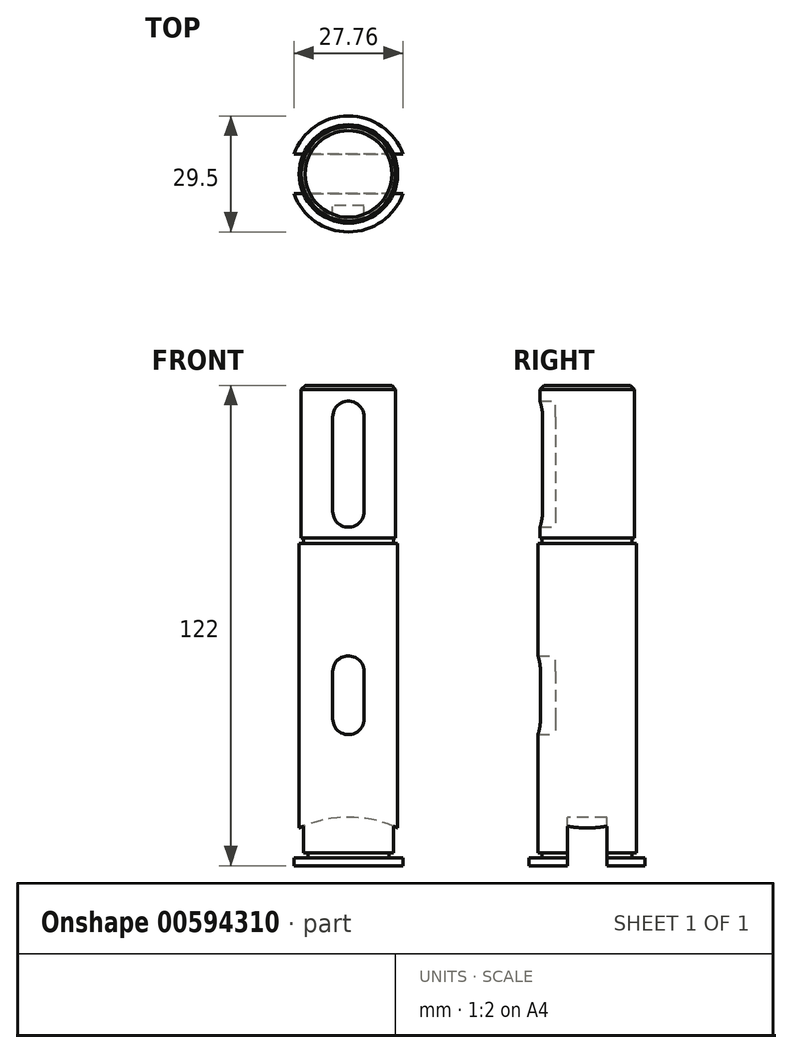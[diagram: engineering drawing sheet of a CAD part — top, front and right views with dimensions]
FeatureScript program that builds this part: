
annotation { "Feature Type Name" : "Feature", "Feature Type Description" : "" }
export const myFeature = defineFeature(function(context is Context, id is Id, definition is map)
    precondition{}
    {
        {
            var Q0;
            Q0=qCreatedBy(makeId("Front.planeOp"),FACE);
            var sketch = newSketch(context, id + "F0", { "sketchPlane" : qUnion([Q0])});
            skLineSegment(sketch, "E0", {"start": v(0, -2) * mm, "end": v(-14.75, -2) * mm});
            skLineSegment(sketch, "E1", {"start": v(-14.75, -2) * mm, "end": v(-14.75, 0) * mm});
            skLineSegment(sketch, "E2", {"start": v(-14.75, 0) * mm, "end": v(-11.45, 0) * mm});
            skLineSegment(sketch, "E3", {"start": v(-11.45, 0) * mm, "end": v(-11.45, 1.3) * mm});
            skLineSegment(sketch, "E4", {"start": v(-11.45, 1.3) * mm, "end": v(-12.5, 1.3) * mm});
            skLineSegment(sketch, "E5", {"start": v(-12.5, 1.3) * mm, "end": v(-12.5, 79.9) * mm});
            skLineSegment(sketch, "E6", {"start": v(-12.5, 79.9) * mm, "end": v(-11.45, 79.9) * mm});
            skLineSegment(sketch, "E7", {"start": v(-11.45, 79.9) * mm, "end": v(-11.45, 81.2) * mm});
            skLineSegment(sketch, "E8", {"start": v(-11.45, 81.2) * mm, "end": v(-12, 81.2) * mm});
            skLineSegment(sketch, "E9", {"start": v(-12, 81.2) * mm, "end": v(-12, 120) * mm});
            skLineSegment(sketch, "E10", {"start": v(-12, 120) * mm, "end": v(0, 120) * mm});
            skLineSegment(sketch, "E11", {"start": v(0, 120) * mm, "end": v(0, -2) * mm});
            skSolve(sketch);
        }
        {
            var Q0;
            Q0=makeQuery(id+"F0.imprint","IMPRINT",FACE,{"disambiguationData":[TD([[makeQuery(id+"F0.imprint","IMPRINT",EDGE,{"derivedFrom":sQuery(id+"F0.wireOp",EDGE,"E0")}),-1.0]])]});
            var Q1;
            Q1=sQuery(id+"F0.wireOp",EDGE,"E11");
            revolve(context, id + "F1", {"entities" : qUnion([Q0]), "axis" : qUnion([Q1]), "revolveType" : RevolveType.FULL});
        }
        {
            var Q0;
            Q0=qCreatedBy(makeId("Front.planeOp"),FACE);
            var sketch = newSketch(context, id + "F2", { "sketchPlane" : qUnion([Q0])});
            skCircle(sketch, "E12", {"center": v(0, -19.7) * mm, "radius": 30 * mm});
            skSolve(sketch);
        }
        {
            var Q0;
            Q0=makeQuery(id+"F2.imprint","IMPRINT",FACE,{"disambiguationData":[TD([[makeQuery(id+"F2.imprint","IMPRINT",EDGE,{"derivedFrom":sQuery(id+"F2.wireOp",EDGE,"E12")}),1.0]])]});
            extrude(context, id + "F3", {"entities" : qUnion([Q0]), "operationType" : NewBodyOperationType.REMOVE, "oppositeDirection" : true, "depth" : 5 * mm, "offsetDistance" : 25 * mm, "hasSecondDirection" : true, "secondDirectionOppositeDirection" : false, "secondDirectionDepth" : 5 * mm});
        }
        {
            var Q0;
            Q0=qCreatedBy(makeId("Front.planeOp"),FACE);
            cPlane(context, id + "F4", {"entities" : qUnion([Q0]), "cplaneType" : CPlaneType.OFFSET, "offset" : 8 * mm, "width" : 150 * mm, "height" : 150 * mm});
        }
        {
            var Q0;
            Q0=qCreatedBy(id+"F4.planeOp",FACE);
            var sketch = newSketch(context, id + "F5", { "sketchPlane" : qUnion([Q0])});
            skLineSegment(sketch, "E13.left", {"start": v(-4, 112) * mm, "end": v(-4, 88) * mm});
            skLineSegment(sketch, "E13.right", {"start": v(4, 112) * mm, "end": v(4, 88) * mm});
            skArc(sketch, "E14", {"start": v(4, 112) * mm, "mid": v(0, 116) * mm, "end": v(-4, 112) * mm});
            skArc(sketch, "E15", {"start": v(-4, 88) * mm, "mid": v(0, 84) * mm, "end": v(4, 88) * mm});
            skSolve(sketch);
        }
        {
            var Q0;
            Q0 = qSketchRegion(id + "F5", true);
            extrude(context, id + "F6", {"entities" : qUnion([Q0]), "operationType" : NewBodyOperationType.REMOVE, "depth" : 25 * mm, "offsetDistance" : 25 * mm});
        }
        {
            var Q0;
            Q0=qCreatedBy(id+"F4.planeOp",FACE);
            var sketch = newSketch(context, id + "F7", { "sketchPlane" : qUnion([Q0])});
            skLineSegment(sketch, "E16.left", {"start": v(-4, 47.3) * mm, "end": v(-4, 35.3) * mm});
            skLineSegment(sketch, "E16.right", {"start": v(4, 47.3) * mm, "end": v(4, 35.3) * mm});
            skArc(sketch, "E17", {"start": v(4, 47.3) * mm, "mid": v(0, 51.3) * mm, "end": v(-4, 47.3) * mm});
            skArc(sketch, "E18", {"start": v(-4, 35.3) * mm, "mid": v(0, 31.3) * mm, "end": v(4, 35.3) * mm});
            skSolve(sketch);
        }
        {
            var Q0;
            Q0 = qSketchRegion(id + "F7", true);
            extrude(context, id + "F8", {"entities" : qUnion([Q0]), "operationType" : NewBodyOperationType.REMOVE, "depth" : 25 * mm, "offsetDistance" : 25 * mm});
        }
        {
            var Q0;
            Q0=makeQuery(id+"F1.opRevolve","SWEPT_EDGE",EDGE,{"disambiguationData":[OSD([sQuery(id+"F0.wireOp",EDGE,"E9"),sQuery(id+"F0.wireOp",EDGE,"E10")])]});
            chamfer(context, id + "F9", {"entities" : qUnion([Q0]), "width" : 1 * mm, "tangentPropagation" : true});
        }
    });
